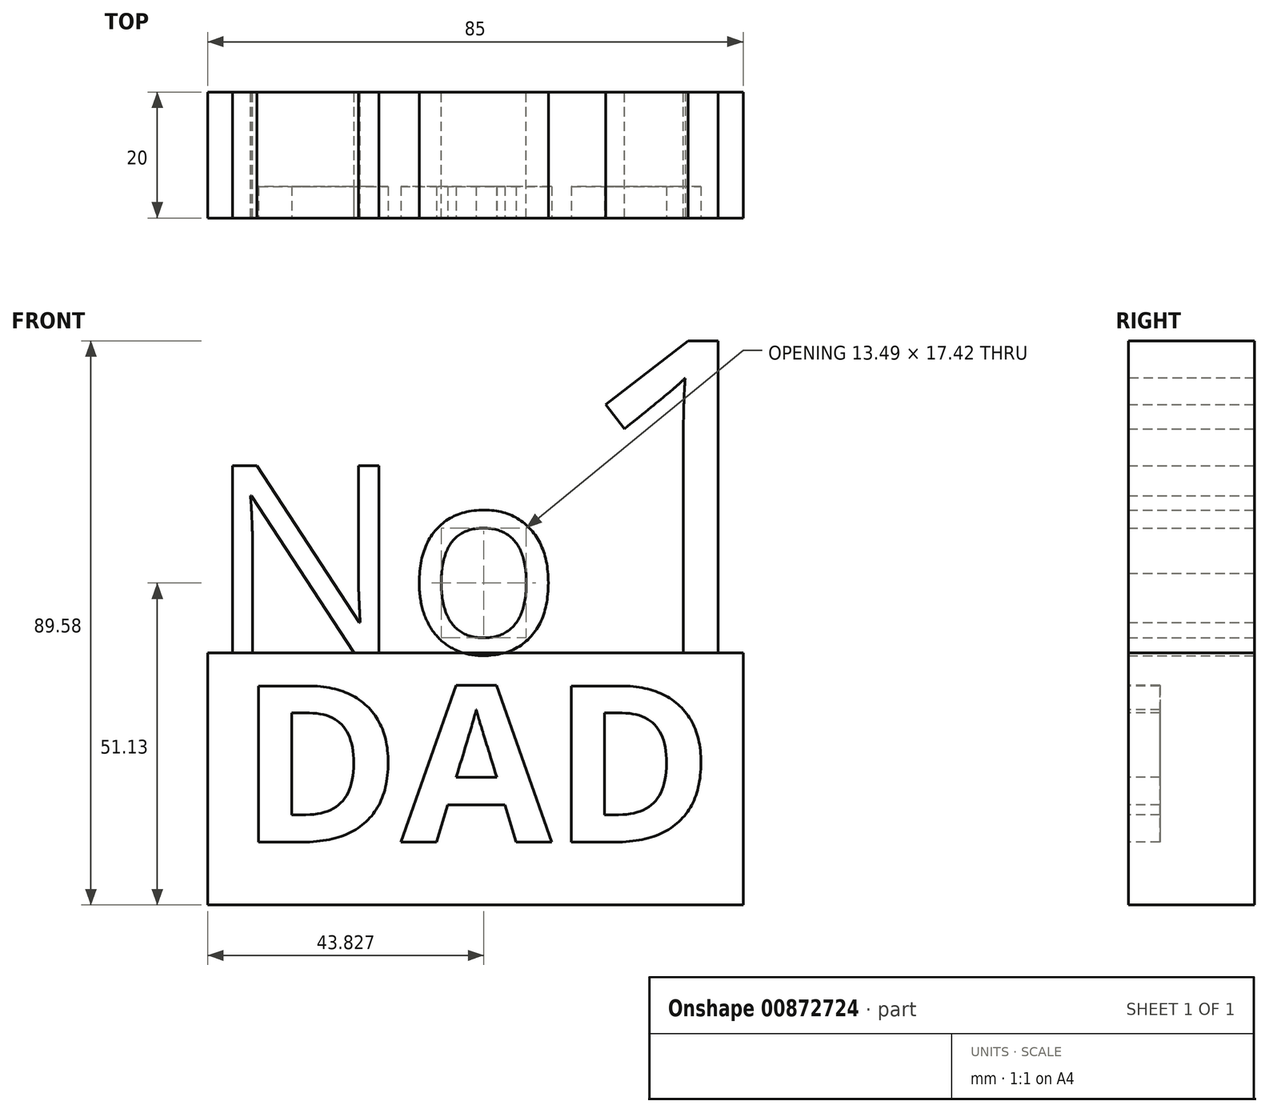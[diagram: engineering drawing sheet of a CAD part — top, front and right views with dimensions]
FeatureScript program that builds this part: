
annotation { "Feature Type Name" : "Feature", "Feature Type Description" : "" }
export const myFeature = defineFeature(function(context is Context, id is Id, definition is map)
    precondition{}
    {
        {
            var Q0;
            Q0=qCreatedBy(makeId("Front.planeOp"),FACE);
            var sketch = newSketch(context, id + "F0", { "sketchPlane" : qUnion([Q0])});
            skText(sketch, "E0", { "text": "No", "fontName": "OpenSans-Regular.ttf"});
            skText(sketch, "E1", { "text": "1", "fontName": "OpenSans-Regular.ttf"});
            const initialGuessF0  = {"E0": [-0.05694, 0, 1, 0, 0.03], "E1": [0, 0, 1, 0, 0.05]};
            skSetInitialGuess(sketch, initialGuessF0);
            skSolve(sketch);
        }
        {
            var Q0;
            Q0=qSketchRegion(id+"F0",true);
            extrude(context, id + "F1", {"entities" : qUnion([Q0]), "endBound" : BoundingType.SYMMETRIC, "depth" : 20 * mm, "offsetDistance" : 25 * mm});
        }
        {
            var Q0;
            Q0=qCreatedBy(makeId("Front.planeOp"),FACE);
            var sketch = newSketch(context, id + "F2", { "sketchPlane" : qUnion([Q0])});
            skLineSegment(sketch, "E2.bottom", {"start": v(-56.77, 0) * mm, "end": v(28.23, 0) * mm});
            skLineSegment(sketch, "E2.top", {"start": v(-56.77, -40) * mm, "end": v(28.23, -40) * mm});
            skLineSegment(sketch, "E2.left", {"start": v(-56.77, 0) * mm, "end": v(-56.77, -40) * mm});
            skLineSegment(sketch, "E2.right", {"start": v(28.23, 0) * mm, "end": v(28.23, -40) * mm});
            skSolve(sketch);
        }
        {
            var Q0;
            Q0=makeQuery(id+"F2.imprint","IMPRINT",FACE,{"disambiguationData":[TD([[makeQuery(id+"F2.imprint","IMPRINT",EDGE,{"derivedFrom":sQuery(id+"F2.wireOp",EDGE,"E2.bottom")}),-1.0]])]});
            extrude(context, id + "F3", {"entities" : qUnion([Q0]), "endBound" : BoundingType.SYMMETRIC, "depth" : 20 * mm, "offsetDistance" : 25 * mm});
        }
        {
            var Q0;
            Q0=makeQuery(id+"F3.opExtrude","CAP_FACE",FACE,{"disambiguationData":[OSD([sQuery(id+"F2.wireOp",EDGE,"E2.bottom"),sQuery(id+"F2.wireOp",EDGE,"E2.top"),sQuery(id+"F2.wireOp",EDGE,"E2.left"),sQuery(id+"F2.wireOp",EDGE,"E2.right")])],"isStart":false});
            var sketch = newSketch(context, id + "F4", { "sketchPlane" : qUnion([Q0])});
            skText(sketch, "E3", { "text": "DAD", "fontName": "OpenSans-Bold.ttf"});
            const initialGuessF4  = {"E3": [-0.05182, -0.03, 1, 0, 0.025]};
            skSetInitialGuess(sketch, initialGuessF4);
            skSolve(sketch);
        }
        {
            var Q0;
            Q0=qSketchRegion(id+"F4",true);
            extrude(context, id + "F5", {"entities" : qUnion([Q0]), "operationType" : NewBodyOperationType.REMOVE, "oppositeDirection" : true, "depth" : 5 * mm, "offsetDistance" : 25 * mm});
        }
    });
